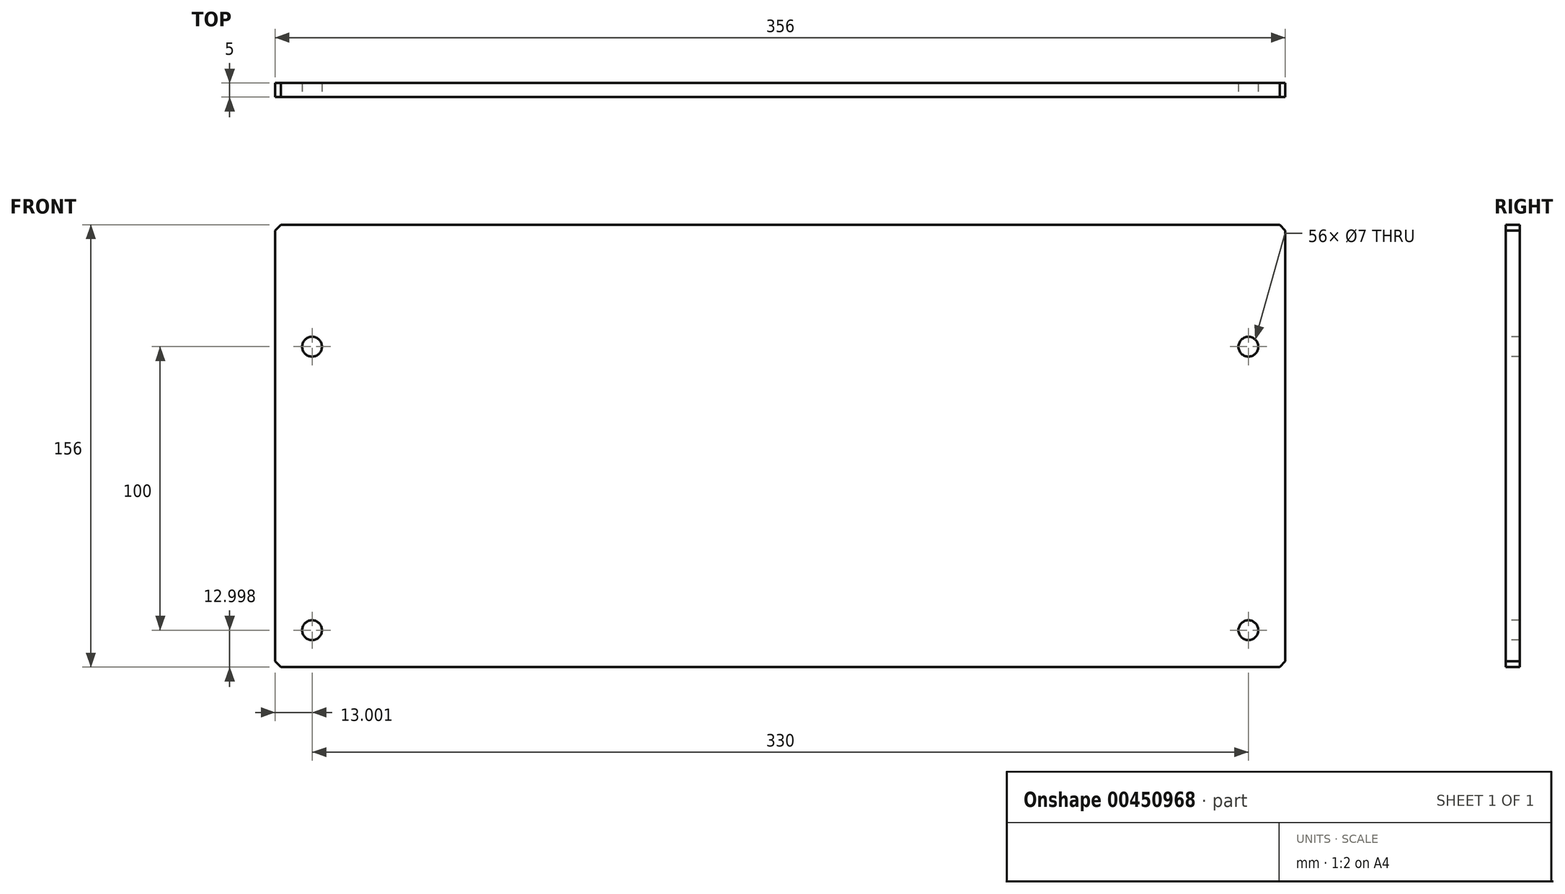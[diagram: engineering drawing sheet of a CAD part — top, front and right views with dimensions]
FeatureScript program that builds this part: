
annotation { "Feature Type Name" : "Feature", "Feature Type Description" : "" }
export const myFeature = defineFeature(function(context is Context, id is Id, definition is map)
    precondition{}
    {
        {
            var Q0;
            Q0=qCreatedBy(makeId("Front.planeOp"),FACE);
            var sketch = newSketch(context, id + "F0", { "sketchPlane" : qUnion([Q0])});
            skLineSegment(sketch, "E0", {"start": v(116.3, -107.9) * mm, "end": v(114.3, -109.9) * mm});
            skLineSegment(sketch, "E1", {"start": v(468.3, -263.9) * mm, "end": v(116.3, -263.9) * mm});
            skLineSegment(sketch, "E2", {"start": v(470.3, -261.9) * mm, "end": v(468.3, -263.9) * mm});
            skLineSegment(sketch, "E3", {"start": v(114.3, -261.9) * mm, "end": v(116.3, -263.9) * mm});
            skLineSegment(sketch, "E4", {"start": v(114.3, -109.9) * mm, "end": v(114.3, -261.9) * mm});
            skLineSegment(sketch, "E5", {"start": v(470.3, -109.9) * mm, "end": v(470.3, -261.9) * mm});
            skLineSegment(sketch, "E6", {"start": v(116.3, -107.9) * mm, "end": v(468.3, -107.9) * mm});
            skLineSegment(sketch, "E7", {"start": v(470.3, -109.9) * mm, "end": v(468.3, -107.9) * mm});
            skLineSegment(sketch, "E8", {"start": v(557.07, -107.9) * mm, "end": v(552.07, -107.9) * mm});
            skLineSegment(sketch, "E9", {"start": v(552.07, -107.9) * mm, "end": v(552.07, -263.9) * mm});
            skLineSegment(sketch, "E10", {"start": v(557.07, -107.9) * mm, "end": v(557.07, -263.9) * mm});
            skLineSegment(sketch, "E11", {"start": v(557.07, -263.9) * mm, "end": v(552.07, -263.9) * mm});
            skCircle(sketch, "E12", {"center": v(457.3, -250.9) * mm, "radius": 3.5 * mm});
            skLineSegment(sketch, "E13", {"start": v(461.84, -250.9) * mm, "end": v(452.74, -250.9) * mm});
            skLineSegment(sketch, "E14", {"start": v(457.3, -246.35) * mm, "end": v(457.3, -255.45) * mm});
            skCircle(sketch, "E15", {"center": v(457.3, -150.9) * mm, "radius": 3.5 * mm});
            skLineSegment(sketch, "E16", {"start": v(461.84, -150.9) * mm, "end": v(452.74, -150.9) * mm});
            skLineSegment(sketch, "E17", {"start": v(457.3, -146.35) * mm, "end": v(457.3, -155.45) * mm});
            skCircle(sketch, "E18", {"center": v(127.3, -150.9) * mm, "radius": 3.5 * mm});
            skLineSegment(sketch, "E19", {"start": v(131.84, -150.9) * mm, "end": v(122.74, -150.9) * mm});
            skLineSegment(sketch, "E20", {"start": v(127.3, -146.35) * mm, "end": v(127.3, -155.45) * mm});
            skCircle(sketch, "E21", {"center": v(127.3, -250.9) * mm, "radius": 3.5 * mm});
            skLineSegment(sketch, "E22", {"start": v(131.84, -250.9) * mm, "end": v(122.74, -250.9) * mm});
            skLineSegment(sketch, "E23", {"start": v(127.3, -246.35) * mm, "end": v(127.3, -255.45) * mm});
            skSolve(sketch);
        }
        {
            var Q0;
            Q0=makeQuery(id+"F0.imprint","IMPRINT",FACE,{"disambiguationData":[TD([[makeQuery(id+"F0.imprint","IMPRINT",EDGE,{"derivedFrom":sQuery(id+"F0.wireOp",EDGE,"E0")}),1.0]])]});
            extrude(context, id + "F1", {"entities" : qUnion([Q0]), "oppositeDirection" : true, "depth" : 5 * mm});
        }
    });
